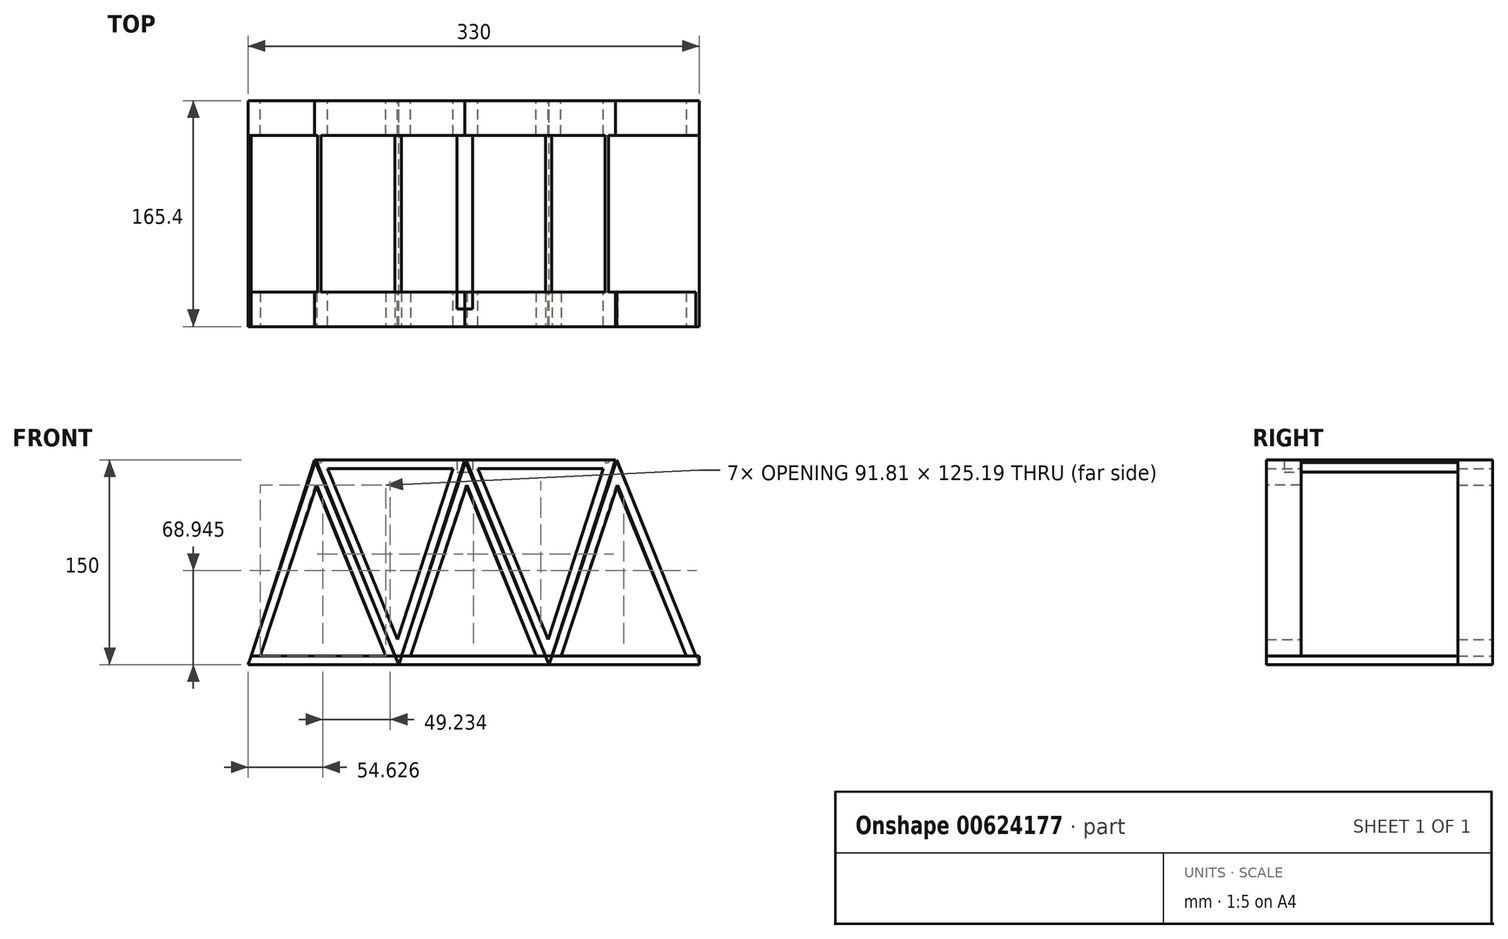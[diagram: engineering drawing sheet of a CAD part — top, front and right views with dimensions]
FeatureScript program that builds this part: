
annotation { "Feature Type Name" : "Feature", "Feature Type Description" : "" }
export const myFeature = defineFeature(function(context is Context, id is Id, definition is map)
    precondition{}
    {
        {
            var Q0;
            Q0=qCreatedBy(makeId("Front.planeOp"),FACE);
            var sketch = newSketch(context, id + "F0", { "sketchPlane" : qUnion([Q0])});
            skLineSegment(sketch, "E0", {"start": v(-269.41, 0) * mm, "end": v(-220.92, 150) * mm});
            skLineSegment(sketch, "E1", {"start": v(-220.92, 150) * mm, "end": v(-159.41, 0) * mm});
            skLineSegment(sketch, "E2", {"start": v(-159.41, 0) * mm, "end": v(-110.92, 150) * mm});
            skLineSegment(sketch, "E3", {"start": v(-110.92, 150) * mm, "end": v(-49.41, 0) * mm});
            skLineSegment(sketch, "E4", {"start": v(-49.41, 0) * mm, "end": v(-0.92, 150) * mm});
            skLineSegment(sketch, "E5", {"start": v(-0.92, 150) * mm, "end": v(60.59, 0) * mm});
            skLineSegment(sketch, "E6", {"start": v(-269.41, 0) * mm, "end": v(-159.41, 0) * mm});
            skLineSegment(sketch, "E7", {"start": v(-49.41, 0) * mm, "end": v(-159.41, 0) * mm});
            skLineSegment(sketch, "E8", {"start": v(-49.41, 0) * mm, "end": v(60.59, 0) * mm});
            skLineSegment(sketch, "E9", {"start": v(-220.92, 150) * mm, "end": v(-110.92, 150) * mm});
            skLineSegment(sketch, "E10", {"start": v(-110.92, 150) * mm, "end": v(-0.92, 150) * mm});
            skLineSegment(sketch, "E11.0", {"start": v(-220.21, 131.54) * mm, "end": v(-168.88, 6.35) * mm});
            skLineSegment(sketch, "E11.1", {"start": v(-260.69, 6.35) * mm, "end": v(-220.21, 131.54) * mm});
            skLineSegment(sketch, "E11.2", {"start": v(-260.69, 6.35) * mm, "end": v(-168.88, 6.35) * mm});
            skLineSegment(sketch, "E12.0", {"start": v(-150.69, 6.35) * mm, "end": v(-110.21, 131.54) * mm});
            skLineSegment(sketch, "E12.1", {"start": v(-58.88, 6.35) * mm, "end": v(-150.69, 6.35) * mm});
            skLineSegment(sketch, "E12.2", {"start": v(-110.21, 131.54) * mm, "end": v(-58.88, 6.35) * mm});
            skLineSegment(sketch, "E13.0", {"start": v(-0.21, 131.54) * mm, "end": v(51.12, 6.35) * mm});
            skLineSegment(sketch, "E13.1", {"start": v(-40.69, 6.35) * mm, "end": v(-0.21, 131.54) * mm});
            skLineSegment(sketch, "E13.2", {"start": v(-40.69, 6.35) * mm, "end": v(51.12, 6.35) * mm});
            skSolve(sketch);
        }
        {
            var Q0;
            Q0=makeQuery(id+"F0.imprint","IMPRINT",FACE,{"disambiguationData":[TD([[makeQuery(id+"F0.imprint","IMPRINT",EDGE,{"derivedFrom":sQuery(id+"F0.wireOp",EDGE,"E0")}),-1.0]])]});
            var Q1;
            Q1=makeQuery(id+"F0.imprint","IMPRINT",FACE,{"disambiguationData":[TD([[makeQuery(id+"F0.imprint","IMPRINT",EDGE,{"derivedFrom":sQuery(id+"F0.wireOp",EDGE,"E2")}),-1.0]])]});
            var Q2;
            Q2=makeQuery(id+"F0.imprint","IMPRINT",FACE,{"disambiguationData":[TD([[makeQuery(id+"F0.imprint","IMPRINT",EDGE,{"derivedFrom":sQuery(id+"F0.wireOp",EDGE,"E4")}),-1.0]])]});
            extrude(context, id + "F1", {"entities" : qUnion([Q0, Q1, Q2]), "depth" : 25.4 * mm, "offsetDistance" : 25.4 * mm});
        }
        {
            var Q0;
            Q0=makeQuery(id+"F1.opExtrude","CAP_FACE",FACE,{"disambiguationData":[OSD([sQuery(id+"F0.wireOp",EDGE,"E0"),sQuery(id+"F0.wireOp",EDGE,"E1"),sQuery(id+"F0.wireOp",EDGE,"E6"),sQuery(id+"F0.wireOp",EDGE,"E11.0"),sQuery(id+"F0.wireOp",EDGE,"E11.1"),sQuery(id+"F0.wireOp",EDGE,"E11.2")])],"isStart":false});
            var sketch = newSketch(context, id + "F2", { "sketchPlane" : qUnion([Q0])});
            skLineSegment(sketch, "E14.bottom", {"start": v(-269.41, 0) * mm, "end": v(60.36, 0) * mm});
            skLineSegment(sketch, "E14.top", {"start": v(-269.41, 6.35) * mm, "end": v(60.36, 6.35) * mm});
            skLineSegment(sketch, "E14.left", {"start": v(-269.41, 0) * mm, "end": v(-269.41, 6.35) * mm});
            skLineSegment(sketch, "E14.right", {"start": v(60.36, 0) * mm, "end": v(60.36, 6.35) * mm});
            skSolve(sketch);
        }
        {
            var Q0;
            {var subQ0=sQuery(id+"F2.wireOp",EDGE,"E14.top");var subQ4=makeQuery(id+"F2.imprint","INTERSECT",VERTEX,{"derivedFrom":[makeQuery(id+"F1.opExtrude","CAP_EDGE",EDGE,{"disambiguationData":[OSD([sQuery(id+"F0.wireOp",EDGE,"E11.1")])],"isStart":false}),subQ0]});Q0=makeQuery(id+"F2.imprint","IMPRINT",FACE,{"disambiguationData":[TD([[makeQuery(id+"F2.imprint","IMPRINT",EDGE,{"disambiguationData":[TD([[subQ4,1.0]])],"derivedFrom":subQ0}),-1.0]])]});}
            var Q1;
            {var subQ3=sQuery(id+"F2.wireOp",EDGE,"E14.right");Q1=makeQuery(id+"F2.imprint","IMPRINT",FACE,{"disambiguationData":[TD([[makeQuery(id+"F2.imprint","IMPRINT",EDGE,{"derivedFrom":subQ3}),1.0]])]});}
            extrude(context, id + "F3", {"entities" : qUnion([Q0, Q1]), "depth" : 140 * mm, "offsetDistance" : 25.4 * mm});
        }
        {
            var Q0;
            Q0=makeQuery(id+"F3.opExtrude","CAP_FACE",FACE,{"disambiguationData":[OSD([sQuery(id+"F0.wireOp",EDGE,"E0"),sQuery(id+"F2.wireOp",EDGE,"E14.bottom"),sQuery(id+"F2.wireOp",EDGE,"E14.top"),sQuery(id+"F2.wireOp",EDGE,"E14.right")])],"isStart":false});
            var sketch = newSketch(context, id + "F4", { "sketchPlane" : qUnion([Q0])});
            skLineSegment(sketch, "E15", {"start": v(-269.41, 0) * mm, "end": v(-220, 149.91) * mm});
            skLineSegment(sketch, "E16", {"start": v(-220, 149.91) * mm, "end": v(-159.41, 0) * mm});
            skLineSegment(sketch, "E17", {"start": v(-159.41, 0) * mm, "end": v(-110, 149.91) * mm});
            skLineSegment(sketch, "E18", {"start": v(-110, 149.91) * mm, "end": v(-49.41, 0) * mm});
            skLineSegment(sketch, "E19", {"start": v(-49.41, 0) * mm, "end": v(0, 149.91) * mm});
            skLineSegment(sketch, "E20", {"start": v(0, 149.91) * mm, "end": v(60.36, 0) * mm});
            skLineSegment(sketch, "E21", {"start": v(-220, 149.91) * mm, "end": v(-110, 149.91) * mm});
            skLineSegment(sketch, "E22", {"start": v(-110, 149.91) * mm, "end": v(0, 149.91) * mm});
            skLineSegment(sketch, "E23", {"start": v(-269.41, 0) * mm, "end": v(-159.41, 0) * mm});
            skLineSegment(sketch, "E24", {"start": v(-159.41, 0) * mm, "end": v(-49.41, 0) * mm});
            skLineSegment(sketch, "E25", {"start": v(-49.41, 0) * mm, "end": v(60.36, 0) * mm});
            skLineSegment(sketch, "E26.0", {"start": v(-260.64, 6.35) * mm, "end": v(-219.4, 131.46) * mm});
            skLineSegment(sketch, "E26.1", {"start": v(-260.64, 6.35) * mm, "end": v(-168.83, 6.35) * mm});
            skLineSegment(sketch, "E26.2", {"start": v(-219.4, 131.46) * mm, "end": v(-168.83, 6.35) * mm});
            skLineSegment(sketch, "E27.0", {"start": v(-150.64, 6.35) * mm, "end": v(-109.4, 131.46) * mm});
            skLineSegment(sketch, "E27.1", {"start": v(-150.64, 6.35) * mm, "end": v(-58.83, 6.35) * mm});
            skLineSegment(sketch, "E27.2", {"start": v(-109.4, 131.46) * mm, "end": v(-58.83, 6.35) * mm});
            skLineSegment(sketch, "E28.0", {"start": v(-40.64, 6.35) * mm, "end": v(0.6, 131.43) * mm});
            skLineSegment(sketch, "E28.1", {"start": v(-40.64, 6.35) * mm, "end": v(50.95, 6.35) * mm});
            skLineSegment(sketch, "E28.2", {"start": v(0.6, 131.43) * mm, "end": v(50.95, 6.35) * mm});
            skSolve(sketch);
        }
        {
            var Q0;
            {var subQ2=sQuery(id+"F4.wireOp",EDGE,"E26.0");Q0=makeQuery(id+"F4.imprint","IMPRINT",FACE,{"disambiguationData":[TD([[makeQuery(id+"F4.imprint","IMPRINT",EDGE,{"derivedFrom":subQ2}),1.0]])]});}
            var Q1;
            {var subQ7=sQuery(id+"F4.wireOp",EDGE,"E27.0");Q1=makeQuery(id+"F4.imprint","IMPRINT",FACE,{"disambiguationData":[TD([[makeQuery(id+"F4.imprint","IMPRINT",EDGE,{"derivedFrom":subQ7}),1.0]])]});}
            var Q2;
            {var subQ0=sQuery(id+"F4.wireOp",EDGE,"E28.0");Q2=makeQuery(id+"F4.imprint","IMPRINT",FACE,{"disambiguationData":[TD([[makeQuery(id+"F4.imprint","IMPRINT",EDGE,{"derivedFrom":subQ0}),1.0]])]});}
            extrude(context, id + "F5", {"entities" : qUnion([Q0, Q1, Q2]), "oppositeDirection" : true, "depth" : 25.4 * mm, "offsetDistance" : 25.4 * mm});
        }
        {
            var Q0;
            Q0=makeQuery(id+"F0.imprint","IMPRINT",FACE,{"disambiguationData":[TD([[makeQuery(id+"F0.imprint","IMPRINT",EDGE,{"derivedFrom":sQuery(id+"F0.wireOp",EDGE,"E1")}),1.0]])]});
            var Q1;
            Q1=makeQuery(id+"F0.imprint","IMPRINT",FACE,{"disambiguationData":[TD([[makeQuery(id+"F0.imprint","IMPRINT",EDGE,{"derivedFrom":sQuery(id+"F0.wireOp",EDGE,"E3")}),1.0]])]});
            var Q2;
            Q2=makeQuery(id+"F5.opExtrude","CAP_FACE",FACE,{"disambiguationData":[OSD([sQuery(id+"F2.wireOp",EDGE,"E14.top"),sQuery(id+"F4.wireOp",EDGE,"E15"),sQuery(id+"F4.wireOp",EDGE,"E16"),sQuery(id+"F4.wireOp",EDGE,"E26.0"),sQuery(id+"F4.wireOp",EDGE,"E26.2")])],"isStart":true});
            extrude(context, id + "F6", {"entities" : qUnion([Q0, Q1]), "endBound" : BoundingType.UP_TO_SURFACE, "depth" : 25.4 * mm, "endBoundEntityFace" : qUnion([Q2]), "offsetDistance" : 25.4 * mm});
        }
        {
            var Q0;
            Q0=makeQuery(id+"F6.opExtrude","CAP_FACE",FACE,{"disambiguationData":[OSD([sQuery(id+"F0.wireOp",EDGE,"E1"),sQuery(id+"F0.wireOp",EDGE,"E2"),sQuery(id+"F0.wireOp",EDGE,"E9")])],"isStart":false});
            var Q1;
            Q1=makeQuery(id+"F6.opExtrude","CAP_FACE",FACE,{"disambiguationData":[OSD([sQuery(id+"F0.wireOp",EDGE,"E3"),sQuery(id+"F0.wireOp",EDGE,"E4"),sQuery(id+"F0.wireOp",EDGE,"E10")])],"isStart":false});
            var Q2;
            Q2=makeQuery(id+"F6.opExtrude","CAP_FACE",FACE,{"disambiguationData":[OSD([sQuery(id+"F0.wireOp",EDGE,"E3"),sQuery(id+"F0.wireOp",EDGE,"E4"),sQuery(id+"F0.wireOp",EDGE,"E10")])],"isStart":true});
            var Q3;
            Q3=makeQuery(id+"F6.opExtrude","CAP_FACE",FACE,{"disambiguationData":[OSD([sQuery(id+"F0.wireOp",EDGE,"E1"),sQuery(id+"F0.wireOp",EDGE,"E2"),sQuery(id+"F0.wireOp",EDGE,"E9")])],"isStart":true});
            shell(context, id + "F7", {"entities" : qUnion([Q0, Q1, Q2, Q3]), "thickness" : 6.35 * mm});
        }
        {
            var Q0;
            Q0=makeQuery(id+"F3.opExtrude","SWEPT_FACE",FACE,{"disambiguationData":[OSD([sQuery(id+"F2.wireOp",EDGE,"E14.right")])]});
            var sketch = newSketch(context, id + "F8", { "sketchPlane" : qUnion([Q0])});
            skLineSegment(sketch, "E29.bottom", {"start": v(-140.04, 6.35) * mm, "end": v(-25.4, 6.35) * mm});
            skLineSegment(sketch, "E29.top", {"start": v(-140.04, 152.12) * mm, "end": v(-25.4, 152.12) * mm});
            skLineSegment(sketch, "E29.left", {"start": v(-140.04, 6.35) * mm, "end": v(-140.04, 152.12) * mm});
            skLineSegment(sketch, "E29.right", {"start": v(-25.4, 6.35) * mm, "end": v(-25.4, 152.12) * mm});
            skSolve(sketch);
        }
        {
            var Q0;
            Q0=makeQuery(id+"F8.imprint","IMPRINT",FACE,{"disambiguationData":[TD([[makeQuery(id+"F8.imprint","IMPRINT",EDGE,{"derivedFrom":sQuery(id+"F8.wireOp",EDGE,"E29.bottom")}),1.0]])]});
            extrude(context, id + "F9", {"entities" : qUnion([Q0]), "operationType" : NewBodyOperationType.REMOVE, "oppositeDirection" : true, "depth" : 333 * mm, "offsetDistance" : 25.4 * mm});
        }
        {
            var Q0;
            {var subQ0=sQuery(id+"F0.wireOp",EDGE,"E1");Q0=makeQuery(id+"F9.boolean.opBoolean","COPY",FACE,{"disambiguationData":[TD([makeQuery(id+"F6.opExtrude","SWEPT_FACE",FACE,{"disambiguationData":[OSD([subQ0])]})])],"derivedFrom":makeQuery(id+"F9.opExtrude","SWEPT_FACE",FACE,{"disambiguationData":[OSD([sQuery(id+"F8.wireOp",EDGE,"E29.right")])]})});}
            var sketch = newSketch(context, id + "F10", { "sketchPlane" : qUnion([Q0])});
            skLineSegment(sketch, "E30.bottom", {"start": v(-218.77, 150) * mm, "end": v(-216.23, 150) * mm});
            skLineSegment(sketch, "E30.top", {"start": v(-218.77, 147.97) * mm, "end": v(-216.23, 147.97) * mm});
            skLineSegment(sketch, "E30.left", {"start": v(-218.77, 150) * mm, "end": v(-218.77, 147.97) * mm});
            skLineSegment(sketch, "E30.right", {"start": v(-216.23, 150) * mm, "end": v(-216.23, 147.97) * mm});
            skSolve(sketch);
        }
        {
            var Q0;
            Q0=makeQuery(id+"F10.imprint","IMPRINT",FACE,{"disambiguationData":[TD([[makeQuery(id+"F10.imprint","IMPRINT",EDGE,{"derivedFrom":sQuery(id+"F10.wireOp",EDGE,"E30.bottom")}),1.0]])]});
            extrude(context, id + "F11", {"entities" : qUnion([Q0]), "operationType" : NewBodyOperationType.ADD, "depth" : 127 * mm, "offsetDistance" : 25.4 * mm});
        }
        {
            var Q0;
            {var subQ0=sQuery(id+"F0.wireOp",EDGE,"E1");Q0=makeQuery(id+"F9.boolean.opBoolean","COPY",FACE,{"disambiguationData":[TD([makeQuery(id+"F6.opExtrude","SWEPT_FACE",FACE,{"disambiguationData":[OSD([subQ0])]})])],"derivedFrom":makeQuery(id+"F9.opExtrude","SWEPT_FACE",FACE,{"disambiguationData":[OSD([sQuery(id+"F8.wireOp",EDGE,"E29.right")])]})});}
            var sketch = newSketch(context, id + "F12", { "sketchPlane" : qUnion([Q0])});
            skLineSegment(sketch, "E31.bottom", {"start": v(-116.86, 150) * mm, "end": v(-105.43, 150) * mm});
            skLineSegment(sketch, "E31.top", {"start": v(-116.86, 141.1) * mm, "end": v(-105.43, 141.1) * mm});
            skLineSegment(sketch, "E31.left", {"start": v(-116.86, 150) * mm, "end": v(-116.86, 141.1) * mm});
            skLineSegment(sketch, "E31.right", {"start": v(-105.43, 150) * mm, "end": v(-105.43, 141.1) * mm});
            skSolve(sketch);
        }
        {
            var Q0;
            {var subQ6=sQuery(id+"F12.wireOp",EDGE,"E31.left");Q0=makeQuery(id+"F12.imprint","IMPRINT",FACE,{"disambiguationData":[TD([[makeQuery(id+"F12.imprint","IMPRINT",EDGE,{"derivedFrom":subQ6}),1.0]])]});}
            var Q1;
            {var subQ3=sQuery(id+"F12.wireOp",EDGE,"E31.right");Q1=makeQuery(id+"F12.imprint","IMPRINT",FACE,{"disambiguationData":[TD([[makeQuery(id+"F12.imprint","IMPRINT",EDGE,{"derivedFrom":subQ3}),-1.0]])]});}
            extrude(context, id + "F13", {"entities" : qUnion([Q0, Q1]), "depth" : 127 * mm, "offsetDistance" : 25.4 * mm});
        }
        {
            var Q0;
            {var subQ0=sQuery(id+"F0.wireOp",EDGE,"E3");Q0=makeQuery(id+"F9.boolean.opBoolean","COPY",FACE,{"disambiguationData":[TD([makeQuery(id+"F6.opExtrude","SWEPT_FACE",FACE,{"disambiguationData":[OSD([subQ0])]})])],"derivedFrom":makeQuery(id+"F9.opExtrude","SWEPT_FACE",FACE,{"disambiguationData":[OSD([sQuery(id+"F8.wireOp",EDGE,"E29.right")])]})});}
            var sketch = newSketch(context, id + "F14", { "sketchPlane" : qUnion([Q0])});
            skLineSegment(sketch, "E32.bottom", {"start": v(-8.33, 150) * mm, "end": v(-5.79, 150) * mm});
            skLineSegment(sketch, "E32.top", {"start": v(-8.33, 147.97) * mm, "end": v(-5.79, 147.97) * mm});
            skLineSegment(sketch, "E32.left", {"start": v(-8.33, 150) * mm, "end": v(-8.33, 147.97) * mm});
            skLineSegment(sketch, "E32.right", {"start": v(-5.79, 150) * mm, "end": v(-5.79, 147.97) * mm});
            skSolve(sketch);
        }
        {
            var Q0;
            Q0=makeQuery(id+"F14.imprint","IMPRINT",FACE,{"disambiguationData":[TD([[makeQuery(id+"F14.imprint","IMPRINT",EDGE,{"derivedFrom":sQuery(id+"F14.wireOp",EDGE,"E32.bottom")}),1.0]])]});
            extrude(context, id + "F15", {"entities" : qUnion([Q0]), "operationType" : NewBodyOperationType.ADD, "depth" : 127 * mm, "offsetDistance" : 25.4 * mm});
        }
    });
